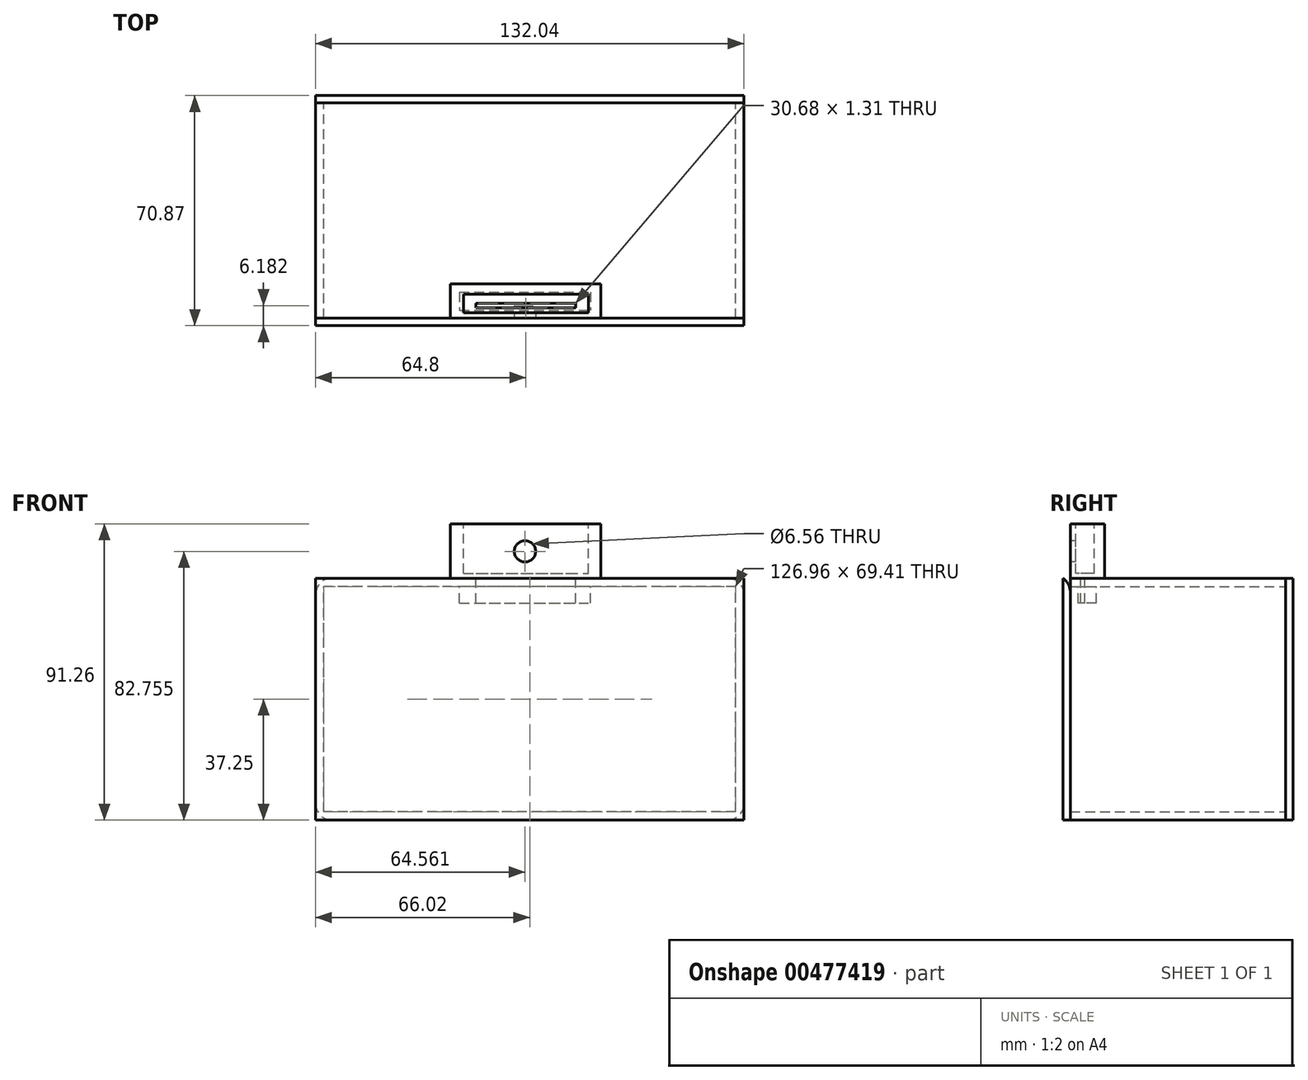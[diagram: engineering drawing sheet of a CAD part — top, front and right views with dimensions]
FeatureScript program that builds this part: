
annotation { "Feature Type Name" : "Feature", "Feature Type Description" : "" }
export const myFeature = defineFeature(function(context is Context, id is Id, definition is map)
    precondition{}
    {
        {
            var Q0;
            Q0=qCreatedBy(makeId("Front.planeOp"),FACE);
            var sketch = newSketch(context, id + "F0", { "sketchPlane" : qUnion([Q0])});
            skLineSegment(sketch, "E0.bottom", {"start": v(66.02, -37.25) * mm, "end": v(-66.02, -37.25) * mm});
            skLineSegment(sketch, "E0.top", {"start": v(66.02, 37.25) * mm, "end": v(-66.02, 37.25) * mm});
            skLineSegment(sketch, "E0.left", {"start": v(66.02, -37.25) * mm, "end": v(66.02, 37.25) * mm});
            skLineSegment(sketch, "E0.right", {"start": v(-66.02, -37.25) * mm, "end": v(-66.02, 37.25) * mm});
            skPoint(sketch, "E0.middle", {"position": v(0, 0) * mm});
            skSolve(sketch);
        }
        {
            var Q0;
            Q0=makeQuery(id+"F0.imprint","IMPRINT",FACE,{"disambiguationData":[TD([[makeQuery(id+"F0.imprint","IMPRINT",EDGE,{"derivedFrom":sQuery(id+"F0.wireOp",EDGE,"E0.bottom")}),-1.0]])]});
            extrude(context, id + "F1", {"entities" : qUnion([Q0]), "depth" : 40.9 * mm});
        }
        {
            var Q0;
            Q0=makeQuery(id+"F1.opExtrude","CAP_FACE",FACE,{"disambiguationData":[OSD([sQuery(id+"F0.wireOp",EDGE,"E0.bottom"),sQuery(id+"F0.wireOp",EDGE,"E0.top"),sQuery(id+"F0.wireOp",EDGE,"E0.left"),sQuery(id+"F0.wireOp",EDGE,"E0.right")])],"isStart":false});
            shell(context, id + "F2", {"entities" : qUnion([Q0]), "thickness" : 2.54 * mm});
        }
        {
            var Q0;
            Q0=makeQuery(id+"F1.opExtrude","CAP_FACE",FACE,{"disambiguationData":[OSD([sQuery(id+"F0.wireOp",EDGE,"E0.bottom"),sQuery(id+"F0.wireOp",EDGE,"E0.top"),sQuery(id+"F0.wireOp",EDGE,"E0.left"),sQuery(id+"F0.wireOp",EDGE,"E0.right")])],"isStart":false});
            var sketch = newSketch(context, id + "F3", { "sketchPlane" : qUnion([Q0])});
            skLineSegment(sketch, "E1.bottom", {"start": v(-66.02, 37.25) * mm, "end": v(66.02, 37.25) * mm});
            skLineSegment(sketch, "E1.top", {"start": v(-66.02, -37.25) * mm, "end": v(66.02, -37.25) * mm});
            skLineSegment(sketch, "E1.left", {"start": v(-66.02, 37.25) * mm, "end": v(-66.02, -37.25) * mm});
            skLineSegment(sketch, "E1.right", {"start": v(66.02, 37.25) * mm, "end": v(66.02, -37.25) * mm});
            skSolve(sketch);
        }
        {
            var Q0;
            Q0 = qSketchRegion(id + "F3", true);
            extrude(context, id + "F4", {"entities" : qUnion([Q0]), "depth" : 2.3 * mm});
        }
        {
            var Q0;
            Q0=makeQuery(id+"F1.opExtrude","CAP_FACE",FACE,{"disambiguationData":[OSD([sQuery(id+"F0.wireOp",EDGE,"E0.bottom"),sQuery(id+"F0.wireOp",EDGE,"E0.top"),sQuery(id+"F0.wireOp",EDGE,"E0.left"),sQuery(id+"F0.wireOp",EDGE,"E0.right")])],"isStart":true});
            extrude(context, id + "F5", {"entities" : qUnion([Q0]), "operationType" : NewBodyOperationType.ADD, "depth" : 25.4 * mm});
        }
        {
            var Q0;
            Q0=makeQuery(id+"F5.opExtrude","CAP_FACE",FACE,{"disambiguationData":[OSD([sQuery(id+"F0.wireOp",EDGE,"E0.bottom"),sQuery(id+"F0.wireOp",EDGE,"E0.top"),sQuery(id+"F0.wireOp",EDGE,"E0.left"),sQuery(id+"F0.wireOp",EDGE,"E0.right")])],"isStart":false});
            shell(context, id + "F6", {"entities" : qUnion([Q0]), "thickness" : 2.54 * mm});
        }
        {
            var Q0;
            Q0=makeQuery(id+"F2.opShell","OFFSET_FACE",FACE,{"disambiguationData":[OSD([sQuery(id+"F0.wireOp",EDGE,"E0.bottom"),sQuery(id+"F0.wireOp",EDGE,"E0.top"),sQuery(id+"F0.wireOp",EDGE,"E0.left"),sQuery(id+"F0.wireOp",EDGE,"E0.right")])]});
            extrude(context, id + "F7", {"entities" : qUnion([Q0]), "operationType" : NewBodyOperationType.REMOVE, "oppositeDirection" : true, "depth" : 92.96 * mm});
        }
        {
            var Q0;
            Q0=makeQuery(id+"F5.opExtrude","CAP_FACE",FACE,{"disambiguationData":[OSD([sQuery(id+"F0.wireOp",EDGE,"E0.bottom"),sQuery(id+"F0.wireOp",EDGE,"E0.top"),sQuery(id+"F0.wireOp",EDGE,"E0.left"),sQuery(id+"F0.wireOp",EDGE,"E0.right")])],"isStart":false});
            var sketch = newSketch(context, id + "F8", { "sketchPlane" : qUnion([Q0])});
            skLineSegment(sketch, "E2.bottom", {"start": v(-66.02, -37.25) * mm, "end": v(66.02, -37.25) * mm});
            skLineSegment(sketch, "E2.top", {"start": v(-66.02, 37.25) * mm, "end": v(66.02, 37.25) * mm});
            skLineSegment(sketch, "E2.left", {"start": v(-66.02, -37.25) * mm, "end": v(-66.02, 37.25) * mm});
            skLineSegment(sketch, "E2.right", {"start": v(66.02, -37.25) * mm, "end": v(66.02, 37.25) * mm});
            skSolve(sketch);
        }
        {
            var Q0;
            Q0 = qSketchRegion(id + "F8", true);
            extrude(context, id + "F9", {"entities" : qUnion([Q0]), "depth" : 2.3 * mm});
        }
        {
            var Q0;
            {var subQ0=sQuery(id+"F0.wireOp",EDGE,"E0.right");var subQ1=sQuery(id+"F0.wireOp",EDGE,"E0.top");Q0=makeQuery(id+"F5.boolean.opBoolean","MERGE",EDGE,{"derivedFrom":[makeQuery(id+"F1.opExtrude","SWEPT_EDGE",EDGE,{"disambiguationData":[OSD([subQ1,subQ0])]}),makeQuery(id+"F5.opExtrude","SWEPT_EDGE",EDGE,{"disambiguationData":[OSD([subQ1,subQ0])]})]});}
            fillet(context, id + "F10", {"entities" : qUnion([Q0]), "radius" : 5.08 * mm, "tangentPropagation" : true, "allowEdgeOverflow" : false});
        }
        {
            var Q0;
            {var subQ0=sQuery(id+"F0.wireOp",EDGE,"E0.right");var subQ1=sQuery(id+"F0.wireOp",EDGE,"E0.bottom");Q0=makeQuery(id+"F5.boolean.opBoolean","MERGE",EDGE,{"derivedFrom":[makeQuery(id+"F1.opExtrude","SWEPT_EDGE",EDGE,{"disambiguationData":[OSD([subQ1,subQ0])]}),makeQuery(id+"F5.opExtrude","SWEPT_EDGE",EDGE,{"disambiguationData":[OSD([subQ1,subQ0])]})]});}
            fillet(context, id + "F11", {"entities" : qUnion([Q0]), "radius" : 5.08 * mm, "tangentPropagation" : true, "allowEdgeOverflow" : false});
        }
        {
            var Q0;
            {var subQ0=sQuery(id+"F0.wireOp",EDGE,"E0.left");var subQ1=sQuery(id+"F0.wireOp",EDGE,"E0.bottom");Q0=makeQuery(id+"F5.boolean.opBoolean","MERGE",EDGE,{"derivedFrom":[makeQuery(id+"F1.opExtrude","SWEPT_EDGE",EDGE,{"disambiguationData":[OSD([subQ1,subQ0])]}),makeQuery(id+"F5.opExtrude","SWEPT_EDGE",EDGE,{"disambiguationData":[OSD([subQ1,subQ0])]})]});}
            fillet(context, id + "F12", {"entities" : qUnion([Q0]), "radius" : 5.08 * mm, "tangentPropagation" : true, "allowEdgeOverflow" : false});
        }
        {
            var Q0;
            {var subQ0=sQuery(id+"F0.wireOp",EDGE,"E0.left");var subQ1=sQuery(id+"F0.wireOp",EDGE,"E0.top");Q0=makeQuery(id+"F5.boolean.opBoolean","MERGE",EDGE,{"derivedFrom":[makeQuery(id+"F1.opExtrude","SWEPT_EDGE",EDGE,{"disambiguationData":[OSD([subQ1,subQ0])]}),makeQuery(id+"F5.opExtrude","SWEPT_EDGE",EDGE,{"disambiguationData":[OSD([subQ1,subQ0])]})]});}
            fillet(context, id + "F13", {"entities" : qUnion([Q0]), "radius" : 5.08 * mm, "tangentPropagation" : true, "allowEdgeOverflow" : false});
        }
        {
            var Q0;
            Q0=makeQuery(id+"F4.opExtrude","CAP_EDGE",EDGE,{"disambiguationData":[OSD([sQuery(id+"F3.wireOp",EDGE,"E1.bottom")])],"isStart":true});
            fillet(context, id + "F14", {"entities" : qUnion([Q0]), "radius" : 5.08 * mm, "tangentPropagation" : true, "allowEdgeOverflow" : false});
        }
        {
            var Q0;
            {var subQ0=sQuery(id+"F0.wireOp",EDGE,"E0.top");Q0=makeQuery(id+"F5.boolean.opBoolean","MERGE",FACE,{"derivedFrom":[makeQuery(id+"F1.opExtrude","SWEPT_FACE",FACE,{"disambiguationData":[OSD([subQ0])]}),makeQuery(id+"F5.opExtrude","SWEPT_FACE",FACE,{"disambiguationData":[OSD([subQ0])]})]});}
            var sketch = newSketch(context, id + "F15", { "sketchPlane" : qUnion([Q0])});
            skLineSegment(sketch, "E3.bottom", {"start": v(-24.44, -30.35) * mm, "end": v(21.87, -30.35) * mm});
            skLineSegment(sketch, "E3.top", {"start": v(-24.44, -40.9) * mm, "end": v(21.87, -40.9) * mm});
            skLineSegment(sketch, "E3.left", {"start": v(-24.44, -30.35) * mm, "end": v(-24.44, -40.9) * mm});
            skLineSegment(sketch, "E3.right", {"start": v(21.87, -30.35) * mm, "end": v(21.87, -40.9) * mm});
            skSolve(sketch);
        }
        {
            var Q0;
            Q0 = qSketchRegion(id + "F15", true);
            extrude(context, id + "F16", {"entities" : qUnion([Q0]), "operationType" : NewBodyOperationType.ADD, "depth" : 16.76 * mm});
        }
        {
            var Q0;
            Q0=makeQuery(id+"F16.opExtrude","CAP_FACE",FACE,{"disambiguationData":[OSD([sQuery(id+"F15.wireOp",EDGE,"E3.bottom"),sQuery(id+"F15.wireOp",EDGE,"E3.top"),sQuery(id+"F15.wireOp",EDGE,"E3.left"),sQuery(id+"F15.wireOp",EDGE,"E3.right")])],"isStart":false});
            var sketch = newSketch(context, id + "F17", { "sketchPlane" : qUnion([Q0])});
            skLineSegment(sketch, "E4.bottom", {"start": v(-21.68, -32.91) * mm, "end": v(18.72, -32.91) * mm});
            skLineSegment(sketch, "E4.top", {"start": v(-21.68, -38.43) * mm, "end": v(18.72, -38.43) * mm});
            skLineSegment(sketch, "E4.left", {"start": v(-21.68, -32.91) * mm, "end": v(-21.68, -38.43) * mm});
            skLineSegment(sketch, "E4.right", {"start": v(18.72, -32.91) * mm, "end": v(18.72, -38.43) * mm});
            skSolve(sketch);
        }
        {
            var Q0;
            Q0 = qSketchRegion(id + "F17", true);
            extrude(context, id + "F18", {"entities" : qUnion([Q0]), "operationType" : NewBodyOperationType.REMOVE, "oppositeDirection" : true, "depth" : 45.47 * mm});
        }
        {
            var Q0;
            Q0=makeQuery(id+"F16.opExtrude","CAP_FACE",FACE,{"disambiguationData":[OSD([sQuery(id+"F15.wireOp",EDGE,"E3.bottom"),sQuery(id+"F15.wireOp",EDGE,"E3.top"),sQuery(id+"F15.wireOp",EDGE,"E3.left"),sQuery(id+"F15.wireOp",EDGE,"E3.right")])],"isStart":false});
            var sketch = newSketch(context, id + "F19", { "sketchPlane" : qUnion([Q0])});
            skLineSegment(sketch, "E5.bottom", {"start": v(-21.68, -32.91) * mm, "end": v(18.72, -32.91) * mm});
            skLineSegment(sketch, "E5.top", {"start": v(-21.68, -38.43) * mm, "end": v(18.72, -38.43) * mm});
            skLineSegment(sketch, "E5.left", {"start": v(-21.68, -32.91) * mm, "end": v(-21.68, -38.43) * mm});
            skLineSegment(sketch, "E5.right", {"start": v(18.72, -32.91) * mm, "end": v(18.72, -38.43) * mm});
            skSolve(sketch);
        }
        {
            var Q0;
            Q0 = qSketchRegion(id + "F19", true);
            extrude(context, id + "F20", {"entities" : qUnion([Q0]), "operationType" : NewBodyOperationType.ADD, "oppositeDirection" : true, "depth" : 24.38 * mm});
        }
        {
            var Q0;
            Q0=makeQuery(id+"F20.boolean.opBoolean","MERGE",FACE,{"derivedFrom":[makeQuery(id+"F16.opExtrude","CAP_FACE",FACE,{"disambiguationData":[OSD([sQuery(id+"F15.wireOp",EDGE,"E3.bottom"),sQuery(id+"F15.wireOp",EDGE,"E3.top"),sQuery(id+"F15.wireOp",EDGE,"E3.left"),sQuery(id+"F15.wireOp",EDGE,"E3.right")])],"isStart":false}),makeQuery(id+"F20.opExtrude","CAP_FACE",FACE,{"disambiguationData":[OSD([sQuery(id+"F19.wireOp",EDGE,"E5.bottom"),sQuery(id+"F19.wireOp",EDGE,"E5.top"),sQuery(id+"F19.wireOp",EDGE,"E5.left"),sQuery(id+"F19.wireOp",EDGE,"E5.right")])],"isStart":true})]});
            var sketch = newSketch(context, id + "F21", { "sketchPlane" : qUnion([Q0])});
            skLineSegment(sketch, "E6.bottom", {"start": v(-20.4, -33.47) * mm, "end": v(18.13, -33.47) * mm});
            skLineSegment(sketch, "E6.top", {"start": v(-20.4, -39.22) * mm, "end": v(18.13, -39.22) * mm});
            skLineSegment(sketch, "E6.left", {"start": v(-20.4, -33.47) * mm, "end": v(-20.4, -39.22) * mm});
            skLineSegment(sketch, "E6.right", {"start": v(18.13, -33.47) * mm, "end": v(18.13, -39.22) * mm});
            skSolve(sketch);
        }
        {
            var Q0;
            Q0 = qSketchRegion(id + "F21", true);
            extrude(context, id + "F22", {"entities" : qUnion([Q0]), "operationType" : NewBodyOperationType.REMOVE, "oppositeDirection" : true, "depth" : 15.24 * mm});
        }
        {
            var Q0;
            Q0=makeQuery(id+"F22.boolean.opBoolean","COPY",FACE,{"derivedFrom":makeQuery(id+"F22.opExtrude","CAP_FACE",FACE,{"disambiguationData":[OSD([sQuery(id+"F21.wireOp",EDGE,"E6.bottom"),sQuery(id+"F21.wireOp",EDGE,"E6.top"),sQuery(id+"F21.wireOp",EDGE,"E6.left"),sQuery(id+"F21.wireOp",EDGE,"E6.right")])],"isStart":false})});
            var sketch = newSketch(context, id + "F23", { "sketchPlane" : qUnion([Q0])});
            skPoint(sketch, "E7.firstSnap0", {"position": v(-20.4, -36.34) * mm});
            skLineSegment(sketch, "E7.bottom", {"start": v(-16.56, -36.34) * mm, "end": v(14.12, -36.34) * mm});
            skLineSegment(sketch, "E7.top", {"start": v(-16.56, -37.65) * mm, "end": v(14.12, -37.65) * mm});
            skLineSegment(sketch, "E7.left", {"start": v(-16.56, -36.34) * mm, "end": v(-16.56, -37.65) * mm});
            skLineSegment(sketch, "E7.right", {"start": v(14.12, -36.34) * mm, "end": v(14.12, -37.65) * mm});
            skSolve(sketch);
        }
        {
            var Q0;
            Q0=makeQuery(id+"F23.imprint","IMPRINT",FACE,{"disambiguationData":[TD([[makeQuery(id+"F23.imprint","IMPRINT",EDGE,{"derivedFrom":sQuery(id+"F23.wireOp",EDGE,"E7.bottom")}),-1.0]])]});
            extrude(context, id + "F24", {"entities" : qUnion([Q0]), "operationType" : NewBodyOperationType.REMOVE, "oppositeDirection" : true, "depth" : 25.4 * mm});
        }
        {
            var Q0;
            Q0=makeQuery(id+"F16.boolean.opBoolean","MERGE",FACE,{"derivedFrom":[makeQuery(id+"F1.opExtrude","CAP_FACE",FACE,{"disambiguationData":[OSD([sQuery(id+"F0.wireOp",EDGE,"E0.bottom"),sQuery(id+"F0.wireOp",EDGE,"E0.top"),sQuery(id+"F0.wireOp",EDGE,"E0.left"),sQuery(id+"F0.wireOp",EDGE,"E0.right")])],"isStart":false}),makeQuery(id+"F16.opExtrude","SWEPT_FACE",FACE,{"disambiguationData":[OSD([sQuery(id+"F15.wireOp",EDGE,"E3.top")])]})]});
            var sketch = newSketch(context, id + "F25", { "sketchPlane" : qUnion([Q0])});
            skCircle(sketch, "E8", {"center": v(-1.46, 45.5) * mm, "radius": 3.28 * mm});
            skSolve(sketch);
        }
        {
            var Q0;
            Q0=makeQuery(id+"F25.imprint","IMPRINT",FACE,{"disambiguationData":[TD([[makeQuery(id+"F25.imprint","IMPRINT",EDGE,{"derivedFrom":sQuery(id+"F25.wireOp",EDGE,"E8")}),1.0]])]});
            extrude(context, id + "F26", {"entities" : qUnion([Q0]), "operationType" : NewBodyOperationType.REMOVE, "oppositeDirection" : true, "depth" : 5.08 * mm});
        }
    });
